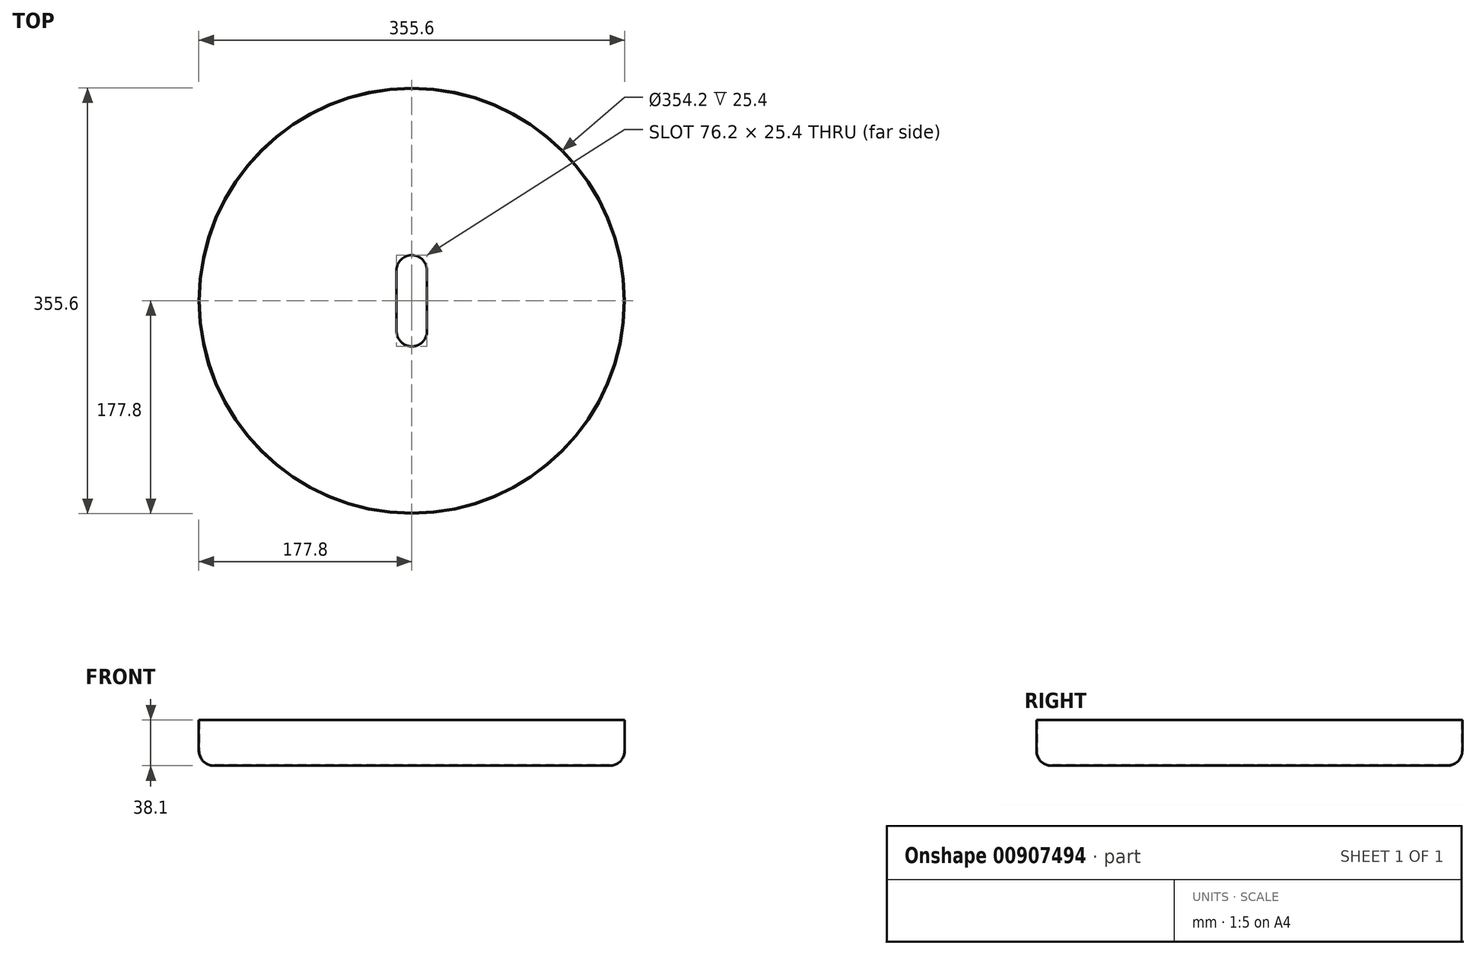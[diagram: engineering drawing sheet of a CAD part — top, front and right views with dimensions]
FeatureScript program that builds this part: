
annotation { "Feature Type Name" : "Feature", "Feature Type Description" : "" }
export const myFeature = defineFeature(function(context is Context, id is Id, definition is map)
    precondition{}
    {
        {
            var Q0;
            Q0=qCreatedBy(makeId("Top.planeOp"),FACE);
            var sketch = newSketch(context, id + "F0", { "sketchPlane" : qUnion([Q0])});
            skCircle(sketch, "E0", {"center": v(0, 0) * mm, "radius": 177.8 * mm});
            skSolve(sketch);
        }
        {
            var Q0;
            Q0 = qSketchRegion(id + "F0", true);
            extrude(context, id + "F1", {"entities" : qUnion([Q0]), "endBound" : BoundingType.SYMMETRIC, "depth" : 38.1 * mm, "offsetDistance" : 25.4 * mm});
        }
        {
            var Q0;
            Q0=makeQuery(id+"F1.opExtrude","CAP_EDGE",EDGE,{"disambiguationData":[OSD([sQuery(id+"F0.wireOp",EDGE,"E0")])],"isStart":true});
            fillet(context, id + "F2", {"entities" : qUnion([Q0]), "radius" : 12.7 * mm, "tangentPropagation" : true, "allowEdgeOverflow" : false});
        }
        {
            var Q0;
            Q0=makeQuery(id+"F1.opExtrude","CAP_FACE",FACE,{"disambiguationData":[OSD([sQuery(id+"F0.wireOp",EDGE,"E0")])],"isStart":false});
            shell(context, id + "F3", {"entities" : qUnion([Q0]), "thickness" : 0.7 * mm});
        }
        {
            var Q0;
            Q0=makeQuery(id+"F1.opExtrude","CAP_FACE",FACE,{"disambiguationData":[OSD([sQuery(id+"F0.wireOp",EDGE,"E0")])],"isStart":true});
            var sketch = newSketch(context, id + "F4", { "sketchPlane" : qUnion([Q0])});
            skArc(sketch, "E1", {"start": v(12.7, 25.33) * mm, "mid": v(0.04, 38.1) * mm, "end": v(-12.7, 25.4) * mm});
            skArc(sketch, "E2", {"start": v(-12.7, -25.4) * mm, "mid": v(0, -38.1) * mm, "end": v(12.7, -25.4) * mm});
            skLineSegment(sketch, "E3", {"start": v(-12.7, 25.4) * mm, "end": v(-12.7, -25.4) * mm});
            skLineSegment(sketch, "E4", {"start": v(12.7, 25.33) * mm, "end": v(12.7, -25.4) * mm});
            skSolve(sketch);
        }
        {
            var Q0;
            Q0=makeQuery(id+"F4.imprint","IMPRINT",FACE,{"disambiguationData":[TD([[makeQuery(id+"F4.imprint","IMPRINT",EDGE,{"derivedFrom":sQuery(id+"F4.wireOp",EDGE,"E1")}),1.0]])]});
            extrude(context, id + "F5", {"entities" : qUnion([Q0]), "operationType" : NewBodyOperationType.REMOVE, "endBound" : BoundingType.SYMMETRIC, "oppositeDirection" : true, "depth" : 25.4 * mm, "offsetDistance" : 25.4 * mm});
        }
    });
